# Revit family: Electric_Water_Heater-Rheem-Induro_Series--
name_source: partatom
category: Mechanical Equipment
units: mm (PartAtom-declared; Revit-internal decimal feet)

## family parameters
Always vertical = Yes
Classification = None
Cut with Voids When Loaded = No
OmniClass Number = 23.65.00.00
OmniClass Title = Supply and Distribution of Liquids and Gases
Part Type = Normal
Room Calculation Point = No
Round Connector Dimension = Use Diameter
Shared = No
Work Plane-Based = No

## types (2) — shared parameters
Assembly Code = D3020
Base Mount Offset From Center = 220 mm  [stored 0.721785 ft]
Cold Water Connection Size = 32 mm
Cold Water Inlet Vertical Offset = 241 mm  [stored 0.790682 ft]
Connector Disk Length = 8 mm  [stored 0.0262467 ft]
Description = Electric Hot Water Heater
ENGworks Global = www.ENGworksGlobal.com
Electric Heat Power = 14400 W
Frequency = 60 Hz
Hot Water Connection Size = 32 mm
Hot Water Flow Return Offset = 879 mm  [stored 2.88386 ft]
Hot Water Outlet Vertical Offset = 1182 mm  [stored 3.87795 ft]
Load Classification = Power
Load Sub-Classification Motor = Yes
Manufacturer = Rheem
Maximum DHW Pressure = 680.0 kPa
Maximum Flow Rate = 315.0 L/s
Maximum Working Pressure = 1000.0 kPa
Number of Poles = 3
Phase = 3
Pipe Offset = 313 mm
Product Page URL = https://www.rheem.com.au
Series = INDURO
TPR Valve Size = 20 mm
TPR Valve Vertical Offset = 1403 mm  [stored 4.60302 ft]
Tank Height = 1748 mm  [stored 5.73491 ft]
Tank Material = Metal - Rheem - Stainless Steel
Tank Outside Diameter = 621 mm  [stored 2.0374 ft]
Tank Outside Radius = 311 mm
Tank Volume = 325.00 L
Top Hook Height = 110 mm  [stored 0.360892 ft]
URL = https://www.rheem.com.au
Unit Weight = 58.000 kgf
Version = 1
Voltage = 400 V
Voltage Comments = 400 VAC
Water Pressure Drop = 0.0 kPa
zero-valued in all types: Default Elevation

## per-type parameters (varying)
| type | Apparent Power | Element Wattage | Full Load Current |
| 6N3315M7 | 10392 VA | 3600 W | 15 A |
| 6N3315M8 | 13856 VA | 4800 W | 20 A |

note: column(s) folded — value = type name in every type: Model

note: [stored X ft] marks values corroborated as IEEE doubles in the binary element streams (Revit-internal decimal feet)

## geometry (parser evidence)
native form markers: Sweep x8
no freeform markers — native parametric forms only
